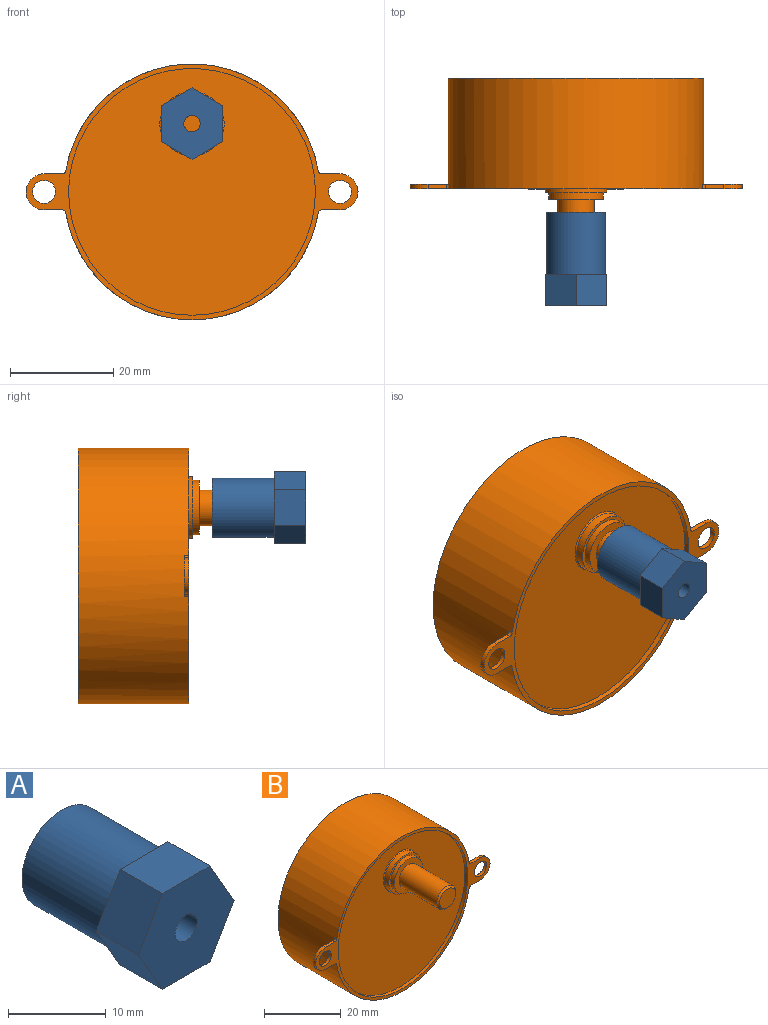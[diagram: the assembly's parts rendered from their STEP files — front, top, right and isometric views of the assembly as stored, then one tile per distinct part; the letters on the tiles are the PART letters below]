
ASSEMBLY  parts=2 mates=1
PART A: 13 faces, bbox 13.8x18x12 mm
  f0: cylinder r=3.49mm len=11.94mm, axis (0,-1,0), area 262mm2, adj f2,f3
  f1: cylinder r=5.74mm len=11.94mm, axis (0,-1,0), area 430.6mm2, adj f2,f12
  f2: plane 11.48x11.48mm, normal (0,1,0), area 65.2mm2, adj f0,f1
  f3: plane 6.99x6.99mm, normal (0,1,0), area 30.4mm2, adj f0,f10
  f4: plane 6.1x5.99mm, normal (0.87,0,0.5), area 42.2mm2, adj f5,f9,f11,f12
  f5: plane 6.92x6.1mm, normal (0,0,1), area 42.2mm2, adj f4,f6,f11,f12
  f6: plane 6.1x5.99mm, normal (-0.87,0,0.5), area 42.2mm2, adj f5,f7,f11,f12
  f7: plane 6.1x5.99mm, normal (-0.87,0,-0.5), area 42.2mm2, adj f6,f8,f11,f12
  f8: plane 6.92x6.1mm, normal (0,0,-1), area 42.2mm2, adj f7,f9,f11,f12
  f9: plane 6.1x5.99mm, normal (0.87,0,-0.5), area 42.2mm2, adj f4,f8,f11,f12
  f10: cylinder r=1.59mm len=6.1mm, axis (0,1,0), area 60.8mm2, adj f3,f11
  f11: plane 13.84x11.99mm, normal (0,-1,0), area 116.6mm2, adj f4,f5,f6,f7,f8,f9,f10
  f12: plane 13.84x11.99mm, normal (0,1,0), area 21mm2, adj f1,f4,f5,f6,f7,f8,f9
PART B: 27 faces, bbox 64.3x37.9x49.5 mm
  f0: cylinder r=5.97mm len=11.94mm, axis (0,1,0), area 58.1mm2, adj f1,f26
  f1: plane 11.94x11.94mm, normal (0,-1,0), area 24.7mm2, adj f0,f2
  f2: cylinder r=5.27mm len=10.54mm, axis (0,1,0), area 42.1mm2, adj f1,f3
  f3: plane 10.54x10.54mm, normal (0,-1,0), area 48.9mm2, adj f2,f4
  f4: cylinder r=3.49mm len=13.97mm, axis (0,1,0), area 306.6mm2, adj f3,f6
  f5: plane 5.97x5.97mm, normal (0,-1,0), area 28mm2, adj f6
  f6: cone r=2.98mm half-angle=45deg, axis (0,1,0), area 14.6mm2, adj f4,f5
  f7: cylinder r=23.88mm len=47.75mm, axis (0,-1,0), area 152.4mm2, adj f8,f25
  f8: plane 47.75x47.75mm, normal (0,-1,0), area 1669.2mm2, adj f7,f26
  f9: plane 8.05x7.7mm, normal (0,1,0), area 31.4mm2, adj f12,f17,f18,f19,f20,f21,f22
  f10: plane 49.53x49.53mm, normal (0,1,0), area 1926.8mm2, adj f22
  f11: plane 8.05x7.7mm, normal (0,1,0), area 31.4mm2, adj f13,f14,f15,f16,f22,f23,f24
  f12: cylinder r=2.22mm len=4.45mm, axis (0,-1,0), area 12.4mm2, adj f9,f25
  f13: cylinder r=2.22mm len=4.45mm, axis (0,-1,0), area 12.4mm2, adj f11,f25
  f14: cylinder r=3.49mm len=6.99mm, axis (0,-1,0), area 9.8mm2, adj f11,f15,f24,f25
  f15: plane 3.58x0.89mm, normal (0,0,1), area 3.2mm2, adj f11,f14,f16,f25
  f16: cylinder r=0.64mm len=0.89mm, axis (0,-1,0), area 0.8mm2, adj f11,f15,f22,f25
  f17: cylinder r=0.64mm len=0.89mm, axis (0,-1,0), area 0.8mm2, adj f9,f18,f22,f25
  f18: plane 3.58x0.89mm, normal (0,0,1), area 3.2mm2, adj f9,f17,f19,f25
  f19: cylinder r=3.49mm len=6.99mm, axis (0,-1,0), area 9.8mm2, adj f9,f18,f20,f25
  f20: plane 3.58x0.89mm, normal (0,0,-1), area 3.2mm2, adj f9,f19,f21,f25
  f21: cylinder r=0.64mm len=0.89mm, axis (0,-1,0), area 0.8mm2, adj f9,f20,f22,f25
  f22: cylinder r=24.77mm len=49.53mm, axis (0,-1,0), area 3305.6mm2, adj f9,f10,f11,f16,f17,f21,f23,f25
  f23: cylinder r=0.64mm len=0.89mm, axis (0,-1,0), area 0.8mm2, adj f11,f22,f24,f25
  f24: plane 3.58x0.89mm, normal (0,0,-1), area 3.2mm2, adj f11,f14,f23,f25
  f25: plane 64.26x49.53mm, normal (0,-1,0), area 198.6mm2, adj f7,f12,f13,f14,f15,f16,f17,f18
  f26: torus R=6.22mm, axis (0,-1,0), area 15.2mm2, adj f0,f8
PLACE A rot(axis=(0,-1,0),90deg) t=(0,-16.54,13.21)mm
PLACE B at identity
MATE fastened A.f0 <-> B.f0  axis (0,1,0) through (0,-16.54,13.21)mm
